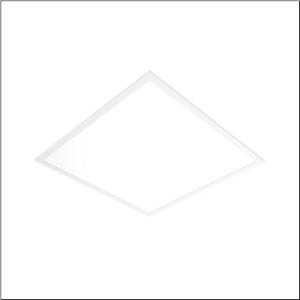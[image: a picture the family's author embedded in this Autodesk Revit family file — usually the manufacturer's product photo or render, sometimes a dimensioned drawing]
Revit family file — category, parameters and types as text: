
# Revit family: apollon_r__41_51mh11w72m43_60bb
name_source: partatom
category: Lighting Fixtures
units: mm (PartAtom-declared; Revit-internal decimal feet)

## family parameters
Cut with Voids When Loaded = No
Host = Face
Light Source = No
Part Type = Normal
Room Calculation Point = No
Round Connector Dimension = Use Diameter
Shared = No

## types (1)
- --- (1 x LED, 3700 lm, 28.5 W, 4000K)
    Apparent Load = 29 VA
    CIE Flux Codes = 61 87 97 100 100
    Color Rendering = 80
    Color Temperature = 4000K
    Default Elevation = 1800 mm
    Description = Apollon® 41, office luminaire, primary optical cover: prismatic diffuser, of PS, light emission: direct distribution, primary light characteristic: symmetric, installation type: lay-in mounting, LED, rated luminous flux: 3.700lm, luminous efficacy: 130lm/W, light colour: 830/840, colour temperature: 3000/4000K, with terminal, 3-pole, mains connection: 220..240V, AC, 50/60Hz, housing, of aluminium section, traffic white (RAL 9016), module: M625, length: 620mm, width: 620mm, height: 28mm, housing upper side, of sheet steel, protection rating (complete): IP20, protection rating (lamp compartment, on room side): IP40, insulation class (complete): insulation class II (safety insulation), certification: CE, ENEC, permissible operating ambient temperature: -25..+40°C, packaging unit: 1 piece
    Height = 0 mm  [stored 0 ft]
    Lamp = 1 x LED
    Lamp Light Flux = 3700 lm
    Lamp Power = 28.5 W
    Lamp count = 1
    Length = 620 mm
    Luminous efficacy = 130 lm/W
    Manufacturer = Siteco
    ModVariant = No
    Model = 51MH11W72M43
    Mounting Place = Ceiling
    Mounting Type = Recessed
    Number of Poles = 1
    OnlyDefault = Yes
    Power Factor = 1
    Product Name = Apollon® 41
    Product group = office luminaire | ceiling recessed
    ProductGroupID = 400
    Protection Class = Protection class II
    Protection Degree = IP 20
    RLX_Detail_Level = 1
    RLX_Emergency_Light_Flux = 0 lm
    RLX_Emergency_Type = 0
    RLX_Emergency_Type_DB = No
    RlxData = <blob elided: 12393 chars, md5=9fc3366b>
    Socket = socket
    Standby Power = 0 W
    System Light Flux = 3700 lm
    System Power = 29 W
    Type Comments = factory setting
    Type Image = l_1291024.jpg
    URL = http://relux.com
    VarID = @adj_045613
    Voltage = 0 V
    Weight = 0.00 kg
    Width = 620 mm

note: [stored X ft] marks values corroborated as IEEE doubles in the binary element streams (Revit-internal decimal feet)

## geometry (parser evidence)
native form markers: Sweep x8
no freeform markers — native parametric forms only
